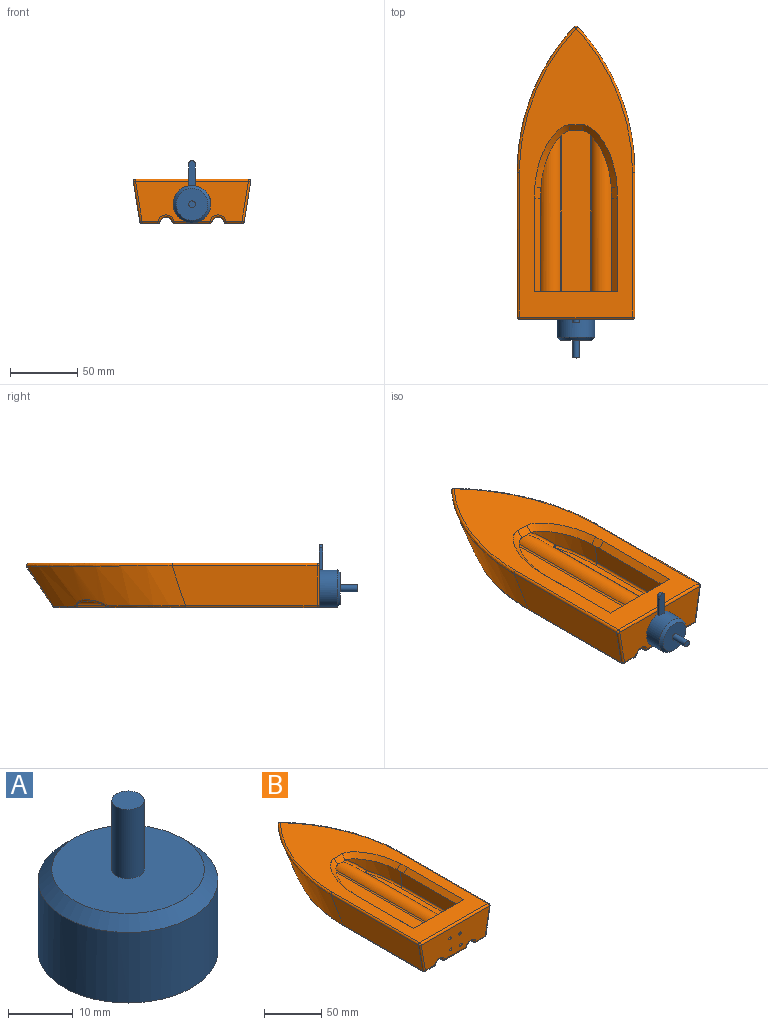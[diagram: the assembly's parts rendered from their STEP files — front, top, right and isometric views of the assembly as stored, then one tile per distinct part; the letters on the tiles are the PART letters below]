
ASSEMBLY  parts=2 mates=1
PART A: 18 faces, bbox 37.7x37.7x28.6 mm
  f0: plane 37.66x37.66mm, normal (0,0,-1), area 673.5mm2, adj f1,f3,f4,f5,f7,f9,f11,f13
  f1: cylinder r=13.95mm len=27.9mm, axis (0,0,-1), area 1160.1mm2, adj f0,f2,f3,f4,f16
  f2: plane 15.78x15.78mm, normal (0,0,1), area 90.4mm2, adj f1,f3,f4,f5
  f3: plane 11.51x11.51mm, normal (0.71,-0.71,0), area 40.7mm2, adj f0,f1,f2,f5
  f4: plane 11.51x11.51mm, normal (-0.71,0.71,0), area 40.7mm2, adj f0,f1,f2,f5
  f5: cylinder r=2.5mm len=4.27mm, axis (0,0,1), area 19.6mm2, adj f0,f2,f3,f4
  f6: plane 3x3mm, normal (0,0,-1), area 7.1mm2, adj f7
  f7: cylinder r=1.5mm len=10mm, axis (0,0,1), area 94.2mm2, adj f0,f6
  f8: plane 3x3mm, normal (0,0,-1), area 7.1mm2, adj f9
  f9: cylinder r=1.5mm len=10mm, axis (0,0,1), area 94.2mm2, adj f0,f8
  f10: plane 3x3mm, normal (0,0,-1), area 7.1mm2, adj f11
  f11: cylinder r=1.5mm len=10mm, axis (0,0,1), area 94.2mm2, adj f0,f10
  f12: plane 3x3mm, normal (0,0,-1), area 7.1mm2, adj f13
  f13: cylinder r=1.5mm len=10mm, axis (0,0,1), area 94.2mm2, adj f0,f12
  f14: cylinder r=2.5mm len=13.1mm, axis (0,0,-1), area 205.8mm2, adj f15,f17
  f15: plane 23.66x23.66mm, normal (0,0,1), area 419.9mm2, adj f14,f16
  f16: cone r=13.95mm half-angle=45deg, axis (0,0,-1), area 243mm2, adj f1,f15
  f17: plane 5x5mm, normal (0,0,1), area 19.6mm2, adj f14
PART B: 112 faces, bbox 96.8x229x45.5 mm
  f0: cylinder r=1.76mm len=20.81mm, axis (-1,0,0), area 57.5mm2, adj f3,f6,f31,f39,f108
  f1: plane 200.24x73.99mm, normal (0,0,-1), area 6623.6mm2, adj f12,f13,f14,f15,f16,f17,f18,f19
  f2: plane 132.55x5.2mm, normal (0,0,1), area 622.1mm2, adj f33,f41,f47,f48
  f3: plane 185.78x20.83mm, normal (0,0,1), area 3725.5mm2, adj f0,f36,f37,f49,f50
  f4: plane 132.55x5.2mm, normal (0,0,1), area 622.1mm2, adj f45,f51,f55,f56
  f5: offset ~228.8x52.8mm, area 2260.9mm2, adj f9,f38,f50,f51,f60,f66
  f6: plane 73.46x20.68mm, normal (0,1,0), area 1304.9mm2, adj f0,f32,f46,f47,f56,f57,f64,f65
  f7: plane 101.45x20.68mm, normal (-0.99,0,0.16), area 2054.6mm2, adj f8,f48,f57,f58
  f8: offset ~228.8x52.8mm, area 2260.9mm2, adj f7,f35,f41,f49,f59,f60
  f9: plane 101.45x20.68mm, normal (0.99,0,0.16), area 2054.6mm2, adj f5,f55,f64,f68
  f10: cylinder r=9.02mm len=171.74mm, axis (0,1,0), area 2641.8mm2, adj f37,f38,f45,f46
  f11: cylinder r=9.02mm len=171.74mm, axis (0,1,0), area 2641.8mm2, adj f32,f33,f35,f36
  f12: plane 61.6x4.4mm, normal (0,1,0), area 251.7mm2, adj f1,f13,f19,f20
  f13: plane 69.12x4.4mm, normal (-0.71,0,0.71), area 430.1mm2, adj f1,f12,f14,f20
  f14: bspline ~8.01x4.61mm, area 49.1mm2, adj f1,f13,f15,f20
  f15: bspline ~46.79x25.81mm, area 331.1mm2, adj f1,f14,f16,f20
  f16: plane 9.54x4.4mm, normal (0,-0.71,0.71), area 59.3mm2, adj f1,f15,f17,f20
  f17: bspline ~46.79x25.81mm, area 331.1mm2, adj f1,f16,f18,f20
  f18: bspline ~8.01x4.61mm, area 49.1mm2, adj f1,f17,f19,f20
  f19: plane 69.12x4.4mm, normal (0.71,0,0.71), area 430.1mm2, adj f1,f12,f18,f20
  f20: plane 215.26x84.83mm, normal (0,0,1), area 8200.2mm2, adj f12,f13,f14,f15,f16,f17,f18,f19
  f21: plane 154.67x11.65mm, normal (0,0,-1), area 1581.1mm2, adj f71,f72,f77,f78
  f22: plane 194.56x26.27mm, normal (0,0,-1), area 4891.8mm2, adj f69,f83,f84,f94,f95
  f23: plane 154.67x11.65mm, normal (0,0,-1), area 1581.1mm2, adj f80,f88,f92,f93
  f24: bspline ~220x44mm, area 3494.7mm2, adj f28,f82,f88,f94,f102,f107
  f25: plane 83.84x29.48mm, normal (0,-1,0), area 2215.1mm2, adj f69,f70,f78,f79,f91,f92,f100,f101
  f26: plane 107.56x29.48mm, normal (0.99,0,-0.16), area 3067.7mm2, adj f27,f77,f91,f99
  f27: bspline ~220x44mm, area 3494.7mm2, adj f26,f72,f85,f95,f102,f103
  f28: plane 107.56x29.48mm, normal (-0.99,0,-0.16), area 3067.7mm2, adj f24,f93,f101,f106
  f29: cylinder r=4.62mm len=177.51mm, axis (0,1,0), area 1981.6mm2, adj f79,f80,f82,f83
  f30: cylinder r=4.62mm len=177.51mm, axis (0,1,0), area 1981.6mm2, adj f70,f71,f84,f85
  f31: sphere r=1.76mm, area 3.4mm2, adj f0,f32,f36
  f32: torus R=10.78mm, axis (0,1,0), area 51.4mm2, adj f6,f11,f31,f40
  f33: cylinder r=1.76mm len=132.54mm, axis (0,1,0), area 224.5mm2, adj f2,f11,f34,f40
  f34: sphere r=1.76mm, area 2mm2, adj f33,f35,f41
  f35: bspline ~43.05x18.75mm, area 114.1mm2, adj f8,f11,f34,f42
  f36: cylinder r=1.76mm len=171.74mm, axis (0,1,0), area 290.9mm2, adj f3,f11,f31,f42
  f37: cylinder r=1.76mm len=171.74mm, axis (0,1,0), area 290.9mm2, adj f3,f10,f39,f43
  f38: bspline ~43.05x18.75mm, area 114.1mm2, adj f5,f10,f43,f44
  f39: sphere r=1.76mm, area 3.4mm2, adj f0,f37,f46
  f40: sphere r=1.76mm, area 3.4mm2, adj f32,f33,f47
  f41: bspline ~47.61x9.13mm, area 92.7mm2, adj f2,f8,f34,f48
  f42: sphere r=1.76mm, area 1mm2, adj f35,f36,f49
  f43: sphere r=1.76mm, area 1mm2, adj f37,f38,f50
  f44: sphere r=1.76mm, area 1.1mm2, adj f38,f45,f51
  f45: cylinder r=1.76mm len=132.54mm, axis (0,1,0), area 224.5mm2, adj f4,f10,f44,f52
  f46: torus R=10.78mm, axis (0,1,0), area 51.4mm2, adj f6,f10,f39,f52
  f47: cylinder r=1.76mm len=5.19mm, axis (-1,0,0), area 14.3mm2, adj f2,f6,f40,f53
  f48: cylinder r=1.76mm len=94.56mm, axis (0,1,0), area 233.9mm2, adj f2,f7,f41,f53
  f49: bspline ~21.13x16.16mm, area 36.6mm2, adj f3,f8,f42,f54
  f50: bspline ~21.13x16.16mm, area 36.6mm2, adj f3,f5,f43,f54
  f51: bspline ~47.61x9.13mm, area 92.7mm2, adj f4,f5,f44,f55
  f52: sphere r=1.76mm, area 3.4mm2, adj f45,f46,f56
  f53: sphere r=1.76mm, area 4.4mm2, adj f47,f48,f57
  f54: sphere r=1.76mm, area 2.8mm2, adj f49,f50,f60
  f55: cylinder r=1.76mm len=94.56mm, axis (0,1,0), area 233.9mm2, adj f4,f9,f51,f61
  f56: cylinder r=1.76mm len=5.19mm, axis (-1,0,0), area 14.3mm2, adj f4,f6,f52,f61
  f57: cylinder r=1.76mm len=20.97mm, axis (0.16,0,0.99), area 58mm2, adj f6,f7,f53,f62
  f58: cylinder r=1.76mm len=101.45mm, axis (0,-1,0), area 310mm2, adj f1,f7,f59,f62
  f59: bspline ~103.36x40.2mm, area 353.7mm2, adj f1,f8,f58,f63
  f60: bspline ~25.05x17.39mm, area 67.5mm2, adj f5,f8,f54,f63
  f61: sphere r=1.76mm, area 2.7mm2, adj f55,f56,f64
  f62: sphere r=1.76mm, area 5.4mm2, adj f57,f58,f65
  f63: sphere r=1.76mm, area 7.4mm2, adj f59,f60,f66
  f64: cylinder r=1.76mm len=20.97mm, axis (0.16,0,-0.99), area 58mm2, adj f6,f9,f61,f67
  f65: cylinder r=1.76mm len=73.46mm, axis (1,0,0), area 203.1mm2, adj f1,f6,f62,f67
  f66: bspline ~103.36x40.2mm, area 353.7mm2, adj f1,f5,f63,f68
  f67: sphere r=1.76mm, area 7.4mm2, adj f64,f65,f68
  f68: cylinder r=1.76mm len=101.45mm, axis (0,-1,0), area 310mm2, adj f1,f9,f66,f67
  f69: cylinder r=1.76mm len=26.24mm, axis (1,0,0), area 72.5mm2, adj f22,f25,f74,f75
  f70: torus R=6.38mm, axis (0,1,0), area 37.6mm2, adj f25,f30,f73,f75
  f71: cylinder r=1.76mm len=154.65mm, axis (0,1,0), area 351.5mm2, adj f21,f30,f73,f76
  f72: bspline ~69.13x17.9mm, area 138.6mm2, adj f21,f27,f76,f77
  f73: sphere r=1.76mm, area 4.2mm2, adj f70,f71,f78
  f74: sphere r=1.76mm, area 4.2mm2, adj f69,f79,f83
  f75: sphere r=1.76mm, area 4mm2, adj f69,f70,f84
  f76: sphere r=1.76mm, area 1.4mm2, adj f71,f72,f85
  f77: cylinder r=1.76mm len=97.73mm, axis (0,-1,0), area 241.8mm2, adj f21,f26,f72,f86
  f78: cylinder r=1.76mm len=11.63mm, axis (1,0,0), area 32.1mm2, adj f21,f25,f73,f86
  f79: torus R=6.38mm, axis (0,1,0), area 37.6mm2, adj f25,f29,f74,f87
  f80: cylinder r=1.76mm len=154.65mm, axis (0,1,0), area 351.5mm2, adj f23,f29,f81,f87
  f81: sphere r=1.76mm, area 1.3mm2, adj f80,f82,f88
  f82: bspline ~24.38x12.65mm, area 71mm2, adj f24,f29,f81,f89
  f83: cylinder r=1.76mm len=177.51mm, axis (0,1,0), area 403.4mm2, adj f22,f29,f74,f89
  f84: cylinder r=1.76mm len=177.51mm, axis (0,1,0), area 403.4mm2, adj f22,f30,f75,f90
  f85: bspline ~24.15x12.58mm, area 71mm2, adj f27,f30,f76,f90
  f86: sphere r=1.76mm, area 4.4mm2, adj f77,f78,f91
  f87: sphere r=1.76mm, area 5.8mm2, adj f79,f80,f92
  f88: bspline ~69.13x17.9mm, area 138.6mm2, adj f23,f24,f81,f93
  f89: sphere r=1.76mm, area 1.2mm2, adj f82,f83,f94
  f90: sphere r=1.76mm, area 0.8mm2, adj f84,f85,f95
  f91: cylinder r=1.76mm len=29.77mm, axis (-0.16,0,-0.99), area 82.6mm2, adj f25,f26,f86,f96
  f92: cylinder r=1.76mm len=11.63mm, axis (1,0,0), area 32.1mm2, adj f23,f25,f87,f97
  f93: cylinder r=1.76mm len=97.73mm, axis (0,-1,0), area 241.8mm2, adj f23,f28,f88,f97
  f94: bspline ~29.34x21.4mm, area 44.8mm2, adj f22,f24,f89,f98
  f95: bspline ~29.34x21.4mm, area 44.8mm2, adj f22,f27,f90,f98
  f96: sphere r=1.76mm, area 3.3mm2, adj f91,f99,f100
  f97: sphere r=1.76mm, area 4.5mm2, adj f92,f93,f101
  f98: sphere r=1.76mm, area 2mm2, adj f94,f95,f102
  f99: cylinder r=1.76mm len=107.56mm, axis (0,1,0), area 328.6mm2, adj f20,f26,f96,f103
  f100: cylinder r=1.76mm len=83.84mm, axis (-1,0,0), area 231.8mm2, adj f20,f25,f96,f104
  f101: cylinder r=1.76mm len=29.77mm, axis (-0.16,0,0.99), area 82.6mm2, adj f25,f28,f97,f104
  f102: bspline ~35.41x24.15mm, area 92.2mm2, adj f24,f27,f98,f105
  f103: bspline ~111.68x45.34mm, area 388.5mm2, adj f20,f27,f99,f105
  f104: sphere r=1.76mm, area 3.5mm2, adj f100,f101,f106
  f105: sphere r=1.76mm, area 5.9mm2, adj f102,f103,f107
  f106: cylinder r=1.76mm len=107.56mm, axis (0,1,0), area 328.6mm2, adj f20,f28,f104,f107
  f107: bspline ~111.68x45.34mm, area 388.5mm2, adj f20,f24,f105,f106
  f108: cylinder r=1.5mm len=4.4mm, axis (0,-1,0), area 41.5mm2, adj f0,f6,f25
  f109: cylinder r=1.5mm len=4.4mm, axis (0,-1,0), area 41.5mm2, adj f6,f25
  f110: cylinder r=1.5mm len=4.4mm, axis (0,-1,0), area 41.5mm2, adj f6,f25
  f111: cylinder r=1.5mm len=4.4mm, axis (0,-1,0), area 41.5mm2, adj f6,f25
PLACE A rot(axis=(0.86,-0.36,0.36),98.4deg) t=(-16.46,-54.32,-0.25)mm
PLACE B t=(0.34,2.04,3.49)mm
MATE fastened A.f11 <-> B.f111  axis (0,1,0) through (-23.17,-54.32,6.46)mm
